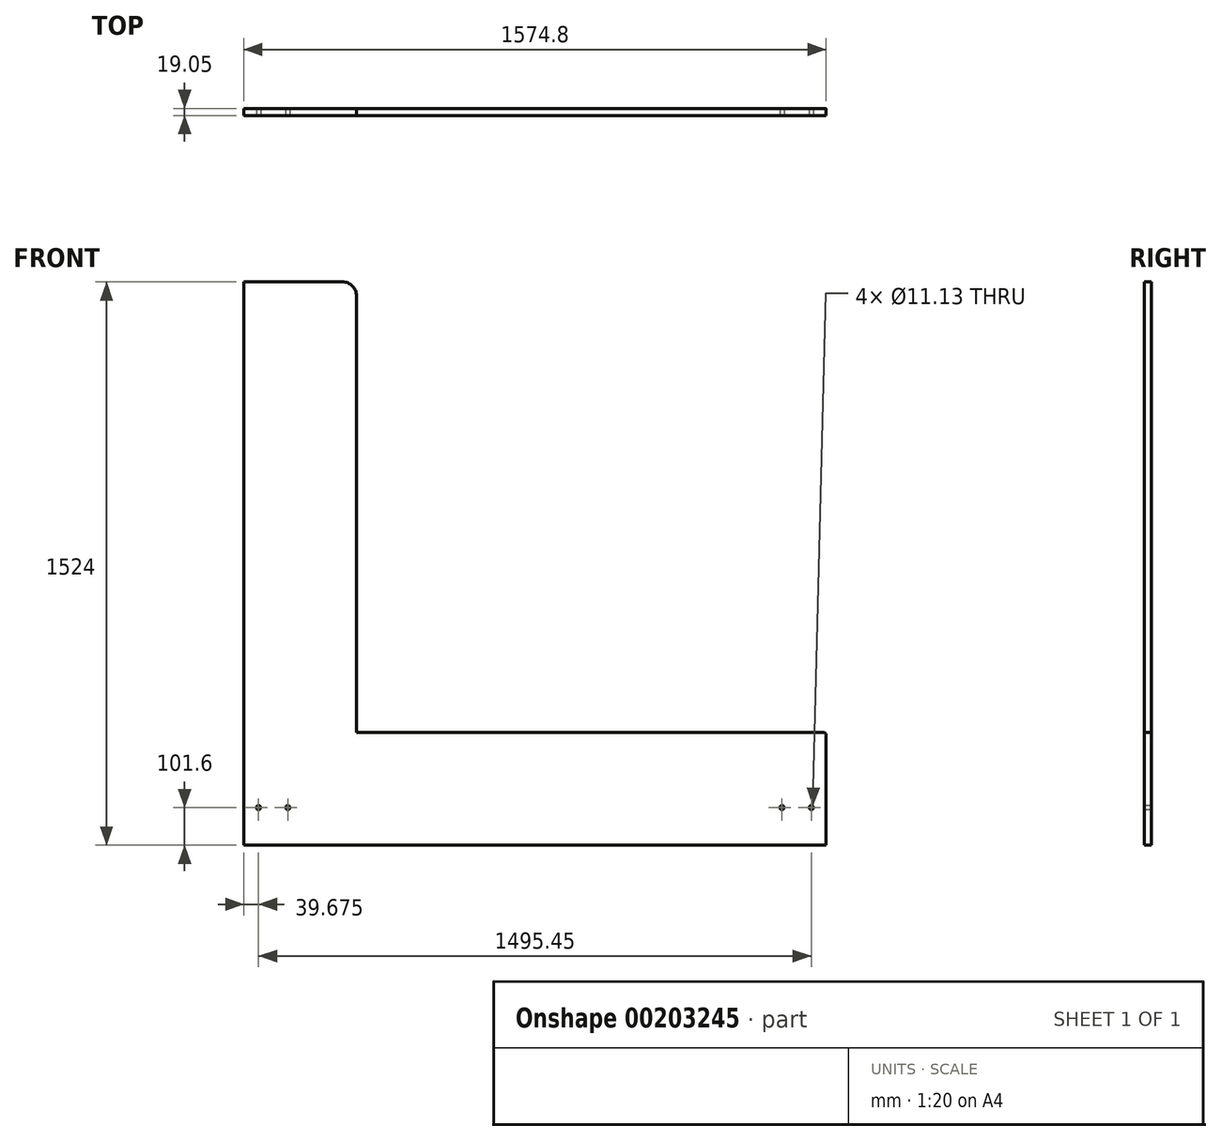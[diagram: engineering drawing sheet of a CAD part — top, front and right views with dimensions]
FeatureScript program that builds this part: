
annotation { "Feature Type Name" : "Feature", "Feature Type Description" : "" }
export const myFeature = defineFeature(function(context is Context, id is Id, definition is map)
    precondition{}
    {
        {
            var Q0;
            Q0=qCreatedBy(makeId("Front.planeOp"),FACE);
            var sketch = newSketch(context, id + "F0", { "sketchPlane" : qUnion([Q0])});
            skLineSegment(sketch, "E0", {"start": v(304.8, 304.8) * mm, "end": v(1371.6, 304.8) * mm});
            skLineSegment(sketch, "E1", {"start": v(1574.8, 304.8) * mm, "end": v(1574.8, 0) * mm});
            skLineSegment(sketch, "E2", {"start": v(1574.8, 0) * mm, "end": v(0, 0) * mm});
            skLineSegment(sketch, "E3", {"start": v(0, 0) * mm, "end": v(0, 1524) * mm});
            skLineSegment(sketch, "E4", {"start": v(0, 1524) * mm, "end": v(266.7, 1524) * mm});
            skLineSegment(sketch, "E5", {"start": v(304.8, 1485.9) * mm, "end": v(304.8, 304.8) * mm});
            skPoint(sketch, "E6.visualSharp", {"position": v(304.8, 1524) * mm});
            skArc(sketch, "E6.filletArc", {"start": v(304.8, 1485.9) * mm, "mid": v(293.64, 1512.84) * mm, "end": v(266.7, 1524) * mm});
            skLineSegment(sketch, "E7", {"start": v(1371.6, 304.8) * mm, "end": v(1574.8, 304.8) * mm});
            skSolve(sketch);
        }
        {
            var Q0;
            Q0 = qSketchRegion(id + "F0", true);
            extrude(context, id + "F1", {"entities" : qUnion([Q0]), "depth" : 19.05 * mm});
        }
        {
            var Q0;
            Q0=makeQuery(id+"F1.opExtrude","SWEPT_EDGE",EDGE,{"disambiguationData":[OSD([sQuery(id+"F0.wireOp",EDGE,"E1"),sQuery(id+"F0.wireOp",EDGE,"E7")])]});
            fillet(context, id + "F2", {"entities" : qUnion([Q0]), "radius" : 6.35 * mm, "tangentPropagation" : true, "allowEdgeOverflow" : false});
        }
        {
            var Q0;
            Q0=makeQuery(id+"F1.opExtrude","CAP_FACE",FACE,{"disambiguationData":[OSD([sQuery(id+"F0.wireOp",EDGE,"E0"),sQuery(id+"F0.wireOp",EDGE,"E1"),sQuery(id+"F0.wireOp",EDGE,"E2"),sQuery(id+"F0.wireOp",EDGE,"E3"),sQuery(id+"F0.wireOp",EDGE,"E4"),sQuery(id+"F0.wireOp",EDGE,"E5"),sQuery(id+"F0.wireOp",EDGE,"E6.filletArc"),sQuery(id+"F0.wireOp",EDGE,"E7")])],"isStart":false});
            var sketch = newSketch(context, id + "F3", { "sketchPlane" : qUnion([Q0])});
            skPoint(sketch, "E8", {"position": v(1535.13, 101.6) * mm});
            skPoint(sketch, "E9", {"position": v(1455.75, 101.6) * mm});
            skPoint(sketch, "E10", {"position": v(119.05, 101.6) * mm});
            skPoint(sketch, "E11", {"position": v(39.67, 101.6) * mm});
            skSolve(sketch);
        }
        {
            var Q0;
            Q0=sQuery(id+"F3.wireOp",VERTEX,"E8");
            var Q1;
            Q1=sQuery(id+"F3.wireOp",VERTEX,"E9");
            var Q2;
            Q2=sQuery(id+"F3.wireOp",VERTEX,"E10");
            var Q3;
            Q3=sQuery(id+"F3.wireOp",VERTEX,"E11");
            var Q4;
            Q4=makeQuery(id+"F1.opExtrude","SWEPT_BODY",BODY,{"disambiguationData":[OSD([sQuery(id+"F0.wireOp",EDGE,"E0"),sQuery(id+"F0.wireOp",EDGE,"E1"),sQuery(id+"F0.wireOp",EDGE,"E2"),sQuery(id+"F0.wireOp",EDGE,"E3"),sQuery(id+"F0.wireOp",EDGE,"E4"),sQuery(id+"F0.wireOp",EDGE,"E5"),sQuery(id+"F0.wireOp",EDGE,"E6.filletArc"),sQuery(id+"F0.wireOp",EDGE,"E7")])]});
            hole(context, id + "F4", {"style" : HoleStyle.SIMPLE, "endStyle" : HoleEndStyle.THROUGH, "holeDiameter" : 11.13 * mm, "startFromSketch" : true, "locations" : qUnion([Q0, Q1, Q2, Q3]), "scope" : qUnion([Q4]), "isTappedThrough" : true});
        }
    });
